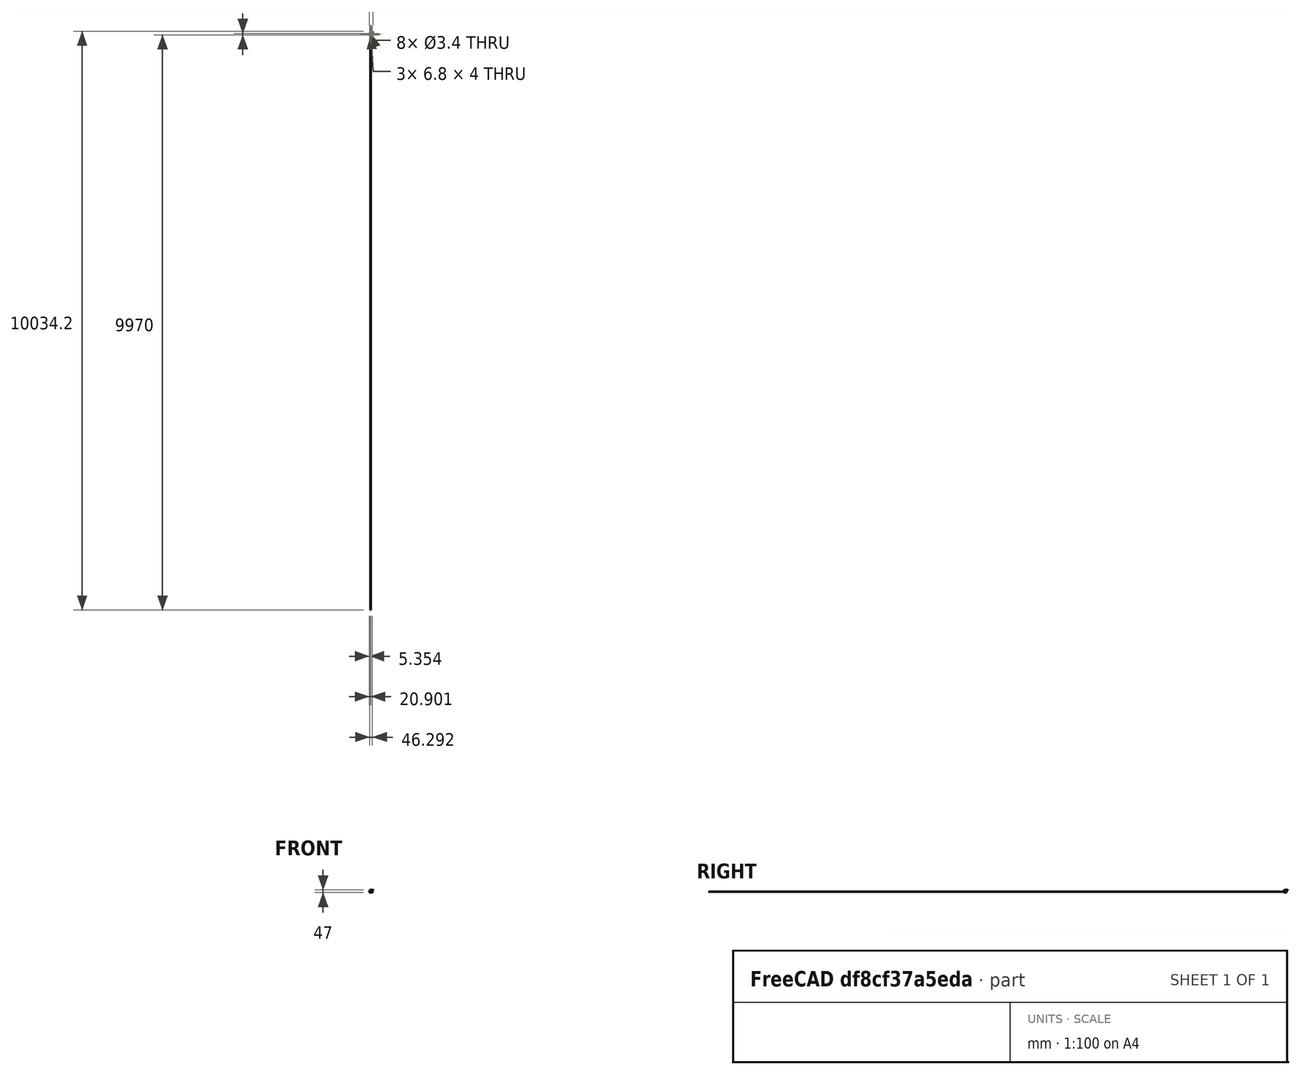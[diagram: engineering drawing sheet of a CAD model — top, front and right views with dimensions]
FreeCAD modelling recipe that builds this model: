
FCSTD DOCUMENT  (FreeCAD 0.14R2935 (Git))
Label: cabeza_cejas
License: CC-BY 3.0
LicenseURL: http://creativecommons.org/licenses/by/3.0/
objects: Sketcher::SketchObject×21, PartDesign::Pocket×15, PartDesign::Chamfer×8, PartDesign::Pad×7, PartDesign::Fillet×6, Part::Box×5, App::DocumentObjectGroup×5, Part::FeaturePython×3, Part::Cylinder×3, Part::Cut×3, Part::Feature×2, Mesh::Feature×1
note: 95 computed .brp shape members not serialized (recipe doc carries the construction recipe); baked Part::Feature solids carry a one-line shape summary decoded from their .brp

FEATURE [Part::Box] Box
  Height = 2
  Length = 10
  Width = 12
FEATURE [Sketcher::SketchObject] Sketch
  Placement = pos=(0,0,2) rot=(0,0,1;0rad)
  Support = -> Box [Face6]
  sketch-geometry (1):
    g0: Circle CenterX=4.90431 CenterY=7.27272 CenterZ=0 NormalX=0 NormalY=0 NormalZ=1 Radius=4.25
  constraints (1):
    c: Radius(g0) = 4.25
FEATURE [PartDesign::Pad] Pad
  Length = 2
  Length2 = 100
  Sketch = -> Sketch
  Type = 0
FEATURE [Sketcher::SketchObject] Sketch001
  ExternalGeometry = -> [Pad]
  Placement = pos=(0,0,4) rot=(0,0,1;0rad)
  Support = -> Pad [Face8]
  sketch-geometry (1):
    g0: Circle CenterX=4.90431 CenterY=7.27272 CenterZ=0 NormalX=0 NormalY=0 NormalZ=1 Radius=2
  constraints (2):
    c: Coincident(g0,g-3)
    c: Radius(g0) = 2
FEATURE [PartDesign::Pocket] Pocket  label="camara"
  Length = 1
  Sketch = -> Sketch001
  Type = 0
FEATURE [App::DocumentObjectGroup] Grupo  label="Camera"
  Group = -> [Box,Pad,Pocket]
FEATURE [Part::FeaturePython] Clone  label="camara001"  # Draft clone (typed FeaturePython)
  Objects = -> [Pocket]
  Placement = pos=(1.5,0,-16) rot=(0,0,1;0rad)
  Scale = (1,1,1)
FEATURE [Part::Cylinder] Cylinder
  Angle = 360
  Height = 2
  Radius = 11.5
FEATURE [Sketcher::SketchObject] Sketch002
  Placement = pos=(0,0,2) rot=(0,0,1;0rad)
  Support = -> Cylinder [Face2]
  sketch-geometry (6):
    g0: LineSegment StartX=-3 StartY=3 StartZ=0 EndX=3 EndY=3 EndZ=0
    g1: LineSegment StartX=3 StartY=3 StartZ=0 EndX=3 EndY=-3 EndZ=0
    g2: LineSegment StartX=3 StartY=-3 StartZ=0 EndX=-3 EndY=-3 EndZ=0
    g3: LineSegment StartX=-3 StartY=-3 StartZ=0 EndX=-3 EndY=3 EndZ=0
    g4: LineSegment [constr] StartX=-3 StartY=3 StartZ=0 EndX=3 EndY=-3 EndZ=0
    g5: LineSegment [constr] StartX=3 StartY=3 StartZ=0 EndX=-3 EndY=-3 EndZ=0
  constraints (16):
    c: Coincident(g0,g1)
    c: Coincident(g1,g2)
    c: Coincident(g2,g3)
    c: Coincident(g3,g0)
    c: Horizontal(g0)
    c: Horizontal(g2)
    c: Vertical(g1)
    c: Vertical(g3)
    c: Equal(g0,g1)
    c: DistanceX(g2) = -6
    c: Coincident(g5,g0)
    c: Coincident(g5,g2)
    c: Coincident(g4,g1)
    c: Coincident(g4,g0)
    c: PointOnObject(g-1,g5)
    c: PointOnObject(g-1,g4)
FEATURE [PartDesign::Pad] Pad001
  Length = 1
  Length2 = 100
  Sketch = -> Sketch002
  Type = 0
FEATURE [Sketcher::SketchObject] Sketch003
  Placement = pos=(0,0,3) rot=(0,0,1;0rad)
  Support = -> Pad001 [Face8]
  sketch-geometry (1):
    g0: Circle CenterX=0 CenterY=0 CenterZ=0 NormalX=0 NormalY=0 NormalZ=1 Radius=2
  constraints (2):
    c: Coincident(g0,g-1)
    c: Radius(g0) = 2
FEATURE [PartDesign::Pocket] Pocket001
  Length = 1
  Sketch = -> Sketch003
  Type = 0
FEATURE [Sketcher::SketchObject] Sketch004
  ExternalGeometry = -> [Pocket001]
  Placement = pos=(0,0,2) rot=(0,0,1;0rad)
  Support = -> Pocket001 [Face2]
  sketch-geometry (28):
    g0: LineSegment StartX=-3 StartY=9.7 StartZ=0 EndX=3 EndY=9.7 EndZ=0
    g1: LineSegment StartX=3 StartY=9.7 StartZ=0 EndX=3 EndY=3.7 EndZ=0
    g2: LineSegment StartX=3 StartY=3.7 StartZ=0 EndX=-3 EndY=3.7 EndZ=0
    g3: LineSegment StartX=-3 StartY=3.7 StartZ=0 EndX=-3 EndY=9.7 EndZ=0
    g4: LineSegment StartX=-9.7 StartY=3 StartZ=0 EndX=-3.7 EndY=3 EndZ=0
    g5: LineSegment StartX=-3.7 StartY=3 StartZ=0 EndX=-3.7 EndY=-3 EndZ=0
    g6: LineSegment StartX=-3.7 StartY=-3 StartZ=0 EndX=-9.7 EndY=-3 EndZ=0
    g7: LineSegment StartX=-9.7 StartY=-3 StartZ=0 EndX=-9.7 EndY=3 EndZ=0
    g8: LineSegment StartX=-3 StartY=-3.7 StartZ=0 EndX=3 EndY=-3.7 EndZ=0
    g9: LineSegment StartX=3 StartY=-3.7 StartZ=0 EndX=3 EndY=-9.7 EndZ=0
    g10: LineSegment StartX=3 StartY=-9.7 StartZ=0 EndX=-3 EndY=-9.7 EndZ=0
    g11: LineSegment StartX=-3 StartY=-9.7 StartZ=0 EndX=-3 EndY=-3.7 EndZ=0
    g12: LineSegment StartX=3.7 StartY=3 StartZ=0 EndX=9.7 EndY=3 EndZ=0
    g13: LineSegment StartX=9.7 StartY=3 StartZ=0 EndX=9.7 EndY=-3 EndZ=0
    g14: LineSegment StartX=9.7 StartY=-3 StartZ=0 EndX=3.7 EndY=-3 EndZ=0
    g15: LineSegment StartX=3.7 StartY=-3 StartZ=0 EndX=3.7 EndY=3 EndZ=0
    g16: LineSegment [constr] StartX=-3 StartY=9.7 StartZ=0 EndX=3 EndY=3.7 EndZ=0
    g17: LineSegment [constr] StartX=3 StartY=9.7 StartZ=0 EndX=-3 EndY=3.7 EndZ=0
    g18: LineSegment [constr] StartX=3.7 StartY=3 StartZ=0 EndX=9.7 EndY=-3 EndZ=0
    g19: LineSegment [constr] StartX=9.7 StartY=3 StartZ=0 EndX=3.7 EndY=-3 EndZ=0
    g20: LineSegment [constr] StartX=-9.7 StartY=3 StartZ=0 EndX=-3.7 EndY=-3 EndZ=0
    g21: LineSegment [constr] StartX=-3.7 StartY=3 StartZ=0 EndX=-9.7 EndY=-3 EndZ=0
    g22: LineSegment [constr] StartX=-3 StartY=-3.7 StartZ=0 EndX=3 EndY=-9.7 EndZ=0
    g23: LineSegment [constr] StartX=3 StartY=-3.7 StartZ=0 EndX=-3 EndY=-9.7 EndZ=0
    g24: GeomPoint [constr] X=0 Y=-6.7 Z=0
    g25: GeomPoint [constr] X=6.7 Y=0 Z=0
    g26: GeomPoint [constr] X=-6.7 Y=0 Z=0
    g27: GeomPoint [constr] X=0 Y=6.7 Z=0
  constraints (72):
    c: Coincident(g0,g1)
    c: Coincident(g1,g2)
    c: Coincident(g2,g3)
    c: Coincident(g3,g0)
    c: Horizontal(g0)
    c: Horizontal(g2)
    c: Vertical(g1)
    c: Vertical(g3)
    c: Equal(g3,g2)
    c: Equal(g2,g-3)
    c: Coincident(g4,g5)
    c: Coincident(g5,g6)
    c: Coincident(g6,g7)
    c: Coincident(g7,g4)
    c: Horizontal(g4)
    c: Horizontal(g6)
    c: Vertical(g5)
    c: Vertical(g7)
    c: Coincident(g8,g9)
    c: Coincident(g9,g10)
    c: Coincident(g10,g11)
    c: Coincident(g11,g8)
    c: Horizontal(g8)
    c: Horizontal(g10)
    c: Vertical(g9)
    c: Vertical(g11)
    c: Coincident(g12,g13)
    c: Coincident(g13,g14)
    c: Coincident(g14,g15)
    c: Coincident(g15,g12)
    c: Horizontal(g12)
    c: Horizontal(g14)
    c: Vertical(g13)
    c: Vertical(g15)
    c: Equal(g12,g15)
    c: Equal(g15,g8)
    c: Equal(g8,g9)
    c: Equal(g9,g6)
    c: Equal(g6,g5)
    c: Equal(g2,g12)
    c: Coincident(g23,g10)
    c: Coincident(g22,g8)
    c: Coincident(g23,g8)
    c: Coincident(g22,g9)
    c: PointOnObject(g24,g-2)
    c: PointOnObject(g24,g23)
    c: PointOnObject(g24,g22)
    c: Coincident(g19,g12)
    c: Coincident(g18,g13)
    c: Coincident(g18,g12)
    c: Coincident(g19,g14)
    c: Coincident(g16,g1)
    c: Coincident(g17,g0)
    c: Coincident(g17,g2)
    c: Coincident(g16,g0)
    c: Coincident(g21,g4)
    c: Coincident(g20,g4)
    c: Coincident(g21,g6)
    c: Coincident(g20,g5)
    c: PointOnObject(g25,g-1)
    c: PointOnObject(g26,g-1)
    c: PointOnObject(g27,g-2)
    c: PointOnObject(g26,g20)
    c: PointOnObject(g26,g21)
    c: PointOnObject(g25,g19)
    c: PointOnObject(g25,g18)
    c: PointOnObject(g27,g16)
    c: PointOnObject(g27,g17)
    c: Distance(g-4,g4) = 0.7
    c: Distance(g-4,g8) = 0.7
    c: Distance(g-5,g14) = 0.7
    c: Distance(g2,g-4) = 0.7
FEATURE [PartDesign::Pad] Pad002
  Length = 1
  Length2 = 100
  Sketch = -> Sketch004
  Type = 0
FEATURE [Sketcher::SketchObject] Sketch005
  ExternalGeometry = -> [Pad002]
  Placement = pos=(0,0,3) rot=(0,0,1;0rad)
  Support = -> Pad002 [Face26]
  sketch-geometry (4):
    g0: Circle CenterX=0 CenterY=6.61559 CenterZ=0 NormalX=0 NormalY=0 NormalZ=1 Radius=2
    g1: Circle CenterX=-6.61558 CenterY=0 CenterZ=0 NormalX=0 NormalY=0 NormalZ=1 Radius=2
    g2: Circle CenterX=6.71215 CenterY=0 CenterZ=0 NormalX=0 NormalY=0 NormalZ=1 Radius=2
    g3: Circle CenterX=0 CenterY=-6.71214 CenterZ=0 NormalX=0 NormalY=0 NormalZ=1 Radius=2
  constraints (8):
    c: Equal(g1,g0)
    c: Equal(g0,g-3)
    c: Equal(g-3,g2)
    c: Equal(g2,g3)
    c: PointOnObject(g2,g-1)
    c: PointOnObject(g0,g-2)
    c: PointOnObject(g1,g-1)
    c: PointOnObject(g3,g-2)
FEATURE [PartDesign::Pocket] Pocket002
  Length = 1
  Sketch = -> Sketch005
  Type = 0
FEATURE [Part::FeaturePython] Clone001  label="ojo001"  # Draft clone (typed FeaturePython)
  Objects = -> [Pocket002]
  Placement = pos=(-7,-6,-13) rot=(0,0,1;0rad)
  Scale = (1,1,1)
FEATURE [App::DocumentObjectGroup] Grupo001  label="ojo"
  Group = -> [Cylinder,Pad001,Pocket001,Pad002,Pocket002]
FEATURE [Part::FeaturePython] Clone002  label="ojo002"  # Draft clone (typed FeaturePython)
  Objects = -> [Pocket002]
  Placement = pos=(21,-7,-13) rot=(0,0,1;0rad)
  Scale = (1,1,1)
FEATURE [Part::Box] Box001
  Height = 4
  Length = 35
  Placement = pos=(-11,-31,-17) rot=(0,0,1;0rad)
  Width = 47
FEATURE [Mesh::Feature] _g_servo  label="9g_servo"
  Placement = pos=(0,-7,-24) rot=(0.57735,0.57735,0.57735;2.0944rad)
FEATURE [Sketcher::SketchObject] Sketch006
  ExternalGeometry = -> [Box001]
  Placement = pos=(-11,-31,-17) rot=(1,0,0;3.14159rad)
  Support = -> Box001 [Face5]
  sketch-geometry (9):
    g0: LineSegment StartX=6.5 StartY=-7.91944 StartZ=0 EndX=13.302 EndY=-7.91944 EndZ=0
    g1: LineSegment StartX=13.302 StartY=-7.91944 StartZ=0 EndX=13.302 EndY=-11.9194 EndZ=0
    g2: LineSegment StartX=13.302 StartY=-11.9194 StartZ=0 EndX=6.5 EndY=-11.9194 EndZ=0
    g3: LineSegment StartX=6.5 StartY=-11.9194 StartZ=0 EndX=6.5 EndY=-7.91944 EndZ=0
    g4: LineSegment StartX=6.5 StartY=-35.9194 StartZ=0 EndX=13.302 EndY=-35.9194 EndZ=0
    g5: LineSegment StartX=13.302 StartY=-35.9194 StartZ=0 EndX=13.302 EndY=-39.9194 EndZ=0
    g6: LineSegment StartX=13.302 StartY=-39.9194 StartZ=0 EndX=6.5 EndY=-39.9194 EndZ=0
    g7: LineSegment StartX=6.5 StartY=-39.9194 StartZ=0 EndX=6.5 EndY=-35.9194 EndZ=0
    g8: LineSegment [constr] StartX=6.5 StartY=0 StartZ=0 EndX=6.5 EndY=-47 EndZ=0
  constraints (27):
    c: Coincident(g0,g1)
    c: Coincident(g1,g2)
    c: Coincident(g2,g3)
    c: Coincident(g3,g0)
    c: Horizontal(g0)
    c: Horizontal(g2)
    c: Vertical(g1)
    c: Vertical(g3)
    c: Coincident(g4,g5)
    c: Coincident(g5,g6)
    c: Coincident(g6,g7)
    c: Coincident(g7,g4)
    c: Horizontal(g4)
    c: Horizontal(g6)
    c: Vertical(g5)
    c: Vertical(g7)
    c: Equal(g2,g4)
    c: Vertical(g8)
    c: PointOnObject(g8,g-3)
    c: PointOnObject(g8,g-1)
    c: PointOnObject(g0,g8)
    c: PointOnObject(g4,g8)
    c: Equal(g1,g5)
    c: DistanceY(g1) = -4
    c: Distance(g2,g4) = 24
    c: Distance(g6,g8) = 7.08056
    c: Distance(g-3,g8) = 6.5
FEATURE [PartDesign::Pad] Pad003
  Length = 14
  Length2 = 100
  Placement = pos=(-11,-31,-17) rot=(0,0,1;0rad)
  Sketch = -> Sketch006
  Type = 0
FEATURE [Sketcher::SketchObject] Sketch007
  ExternalGeometry = -> [Pad003]
  Placement = pos=(2.30204,-31,-17) rot=(0.57735,0.57735,0.57735;2.0944rad)
  Support = -> Pad003 [Face7]
  sketch-geometry (3):
    g0: Circle CenterX=9.93523 CenterY=-7.03791 CenterZ=0 NormalX=0 NormalY=0 NormalZ=1 Radius=1.64716
    g1: Circle CenterX=37.8885 CenterY=-7.03791 CenterZ=0 NormalX=0 NormalY=0 NormalZ=1 Radius=1.53113
    g2: LineSegment [constr] StartX=35.9194 StartY=-7.03791 StartZ=0 EndX=11.9194 EndY=-7.03791 EndZ=0
  constraints (5):
    c: PointOnObject(g2,g-3)
    c: Horizontal(g2)
    c: PointOnObject(g2,g-4)
    c: PointOnObject(g0,g2)
    c: PointOnObject(g1,g2)
FEATURE [PartDesign::Pocket] Pocket003
  Length = 7
  Placement = pos=(-11,-31,-17) rot=(0,0,1;0rad)
  Sketch = -> Sketch007
  Type = 0
FEATURE [Sketcher::SketchObject] Sketch008
  ExternalGeometry = -> [Pocket003]
  Placement = pos=(-11,-31,-17) rot=(1,0,0;3.14159rad)
  Support = -> Pocket003 [Face5]
  sketch-geometry (6):
    g0: ArcOfCircle CenterX=31.6459 CenterY=-23.9498 CenterZ=0 NormalX=0 NormalY=0 NormalZ=1 Radius=11.5 StartAngle=5.00835 EndAngle=7.55802
    g1: LineSegment [constr] StartX=35 StartY=-12.9498 StartZ=0 EndX=0 EndY=-12.9498 EndZ=0
    g2: LineSegment [constr] StartX=35 StartY=-34.9498 StartZ=0 EndX=0 EndY=-34.9498 EndZ=0
    g3: ArcOfCircle CenterX=3.3541 CenterY=-23.9498 CenterZ=0 NormalX=0 NormalY=0 NormalZ=1 Radius=11.5 StartAngle=1.86676 EndAngle=4.41643
    g4: LineSegment StartX=35 StartY=-12.9498 StartZ=0 EndX=35 EndY=-34.9498 EndZ=0
    g5: LineSegment StartX=0 StartY=-12.9498 StartZ=0 EndX=0 EndY=-34.9498 EndZ=0
  constraints (20):
    c: PointOnObject(g0,g-3)
    c: PointOnObject(g0,g-3)
    c: Distance(g0,g0) = 22
    c: Radius(g0) = 11.5
    c: Horizontal(g1)
    c: Horizontal(g2)
    c: Distance(g-3,g0) = 12.9498
    c: Coincident(g1,g0)
    c: PointOnObject(g1,g-2)
    c: Coincident(g2,g0)
    c: PointOnObject(g2,g-2)
    c: Coincident(g3,g2)
    c: Coincident(g3,g1)
    c: Equal(g0,g3)
    c: Vertical(g4)
    c: Coincident(g4,g0)
    c: Coincident(g4,g0)
    c: Vertical(g5)
    c: Coincident(g5,g1)
    c: Coincident(g5,g2)
FEATURE [PartDesign::Pad] Pad004
  Length = 4
  Length2 = 100
  Placement = pos=(-11,-31,-17) rot=(0,0,1;0rad)
  Reversed = true
  Sketch = -> Sketch008
  Type = 0
FEATURE [Sketcher::SketchObject] Sketch009
  ExternalGeometry = -> [Pad004]
  Placement = pos=(-11,-31,-13) rot=(0,0,1;0rad)
  Support = -> Pad004 [Face4]
  sketch-geometry (6):
    g0: Circle CenterX=17.5 CenterY=38.5843 CenterZ=0 NormalX=0 NormalY=0 NormalZ=1 Radius=4.5
    g1: LineSegment [constr] StartX=0 StartY=38.5843 StartZ=0 EndX=17.5 EndY=38.5843 EndZ=0
    g2: LineSegment [constr] StartX=17.5 StartY=38.5843 StartZ=0 EndX=35 EndY=38.5843 EndZ=0
    g3: Circle CenterX=-5.6459 CenterY=23.9498 CenterZ=0 NormalX=0 NormalY=0 NormalZ=1 Radius=1.7
    g4: Circle CenterX=40.6459 CenterY=23.9498 CenterZ=0 NormalX=0 NormalY=0 NormalZ=1 Radius=1.7
    g5: LineSegment [constr] StartX=-8.1459 StartY=23.9498 StartZ=0 EndX=43.1459 EndY=23.9498 EndZ=0
  constraints (19):
    c: Horizontal(g1)
    c: Horizontal(g2)
    c: PointOnObject(g1,g-2)
    c: PointOnObject(g2,g-3)
    c: Coincident(g2,g0)
    c: Coincident(g1,g0)
    c: Equal(g1,g2)
    c: Radius(g0) = 4.5
    c: DistanceY(g-1,g2) = 38.5843
    c: Horizontal(g5)
    c: PointOnObject(g5,g-5)
    c: PointOnObject(g5,g-4)
    c: PointOnObject(g3,g5)
    c: PointOnObject(g4,g5)
    c: Radius(g4) = 1.7
    c: Radius(g3) = 1.7
    c: Distance(g3,g5) = 2.5
    c: Distance(g4,g5) = 2.5
    c: PointOnObject(g-5,g5)
FEATURE [PartDesign::Pocket] Pocket004
  Length = 4
  Placement = pos=(-11,-31,-17) rot=(0,0,1;0rad)
  Sketch = -> Sketch009
  Type = 0
FEATURE [Part::Feature] Pocket004001  label="Pocket005"
  shape: bbox 51.29 x 47 x 18 mm, 26 faces (baked)
FEATURE [PartDesign::Chamfer] Chamfer
  Base = -> Pocket004001 [Edge6]
  Size = 10
FEATURE [PartDesign::Chamfer] Chamfer001
  Base = -> Chamfer [Edge3]
  Size = 10
FEATURE [PartDesign::Fillet] Fillet
  Base = -> Chamfer001 [Edge3]
  Radius = 10
FEATURE [PartDesign::Fillet] Fillet001
  Base = -> Fillet [Edge3]
  Radius = 10
FEATURE [PartDesign::Fillet] Fillet002
  Base = -> Fillet001 [Edge45]
  Radius = 3
FEATURE [PartDesign::Fillet] Fillet003
  Base = -> Fillet002 [Edge43]
  Radius = 3
FEATURE [PartDesign::Chamfer] Chamfer002
  Base = -> Fillet003 [Edge46]
  Size = 10
FEATURE [PartDesign::Chamfer] Chamfer003
  Base = -> Chamfer002 [Edge29]
  Size = 10
FEATURE [Sketcher::SketchObject] Sketch010
  ExternalGeometry = -> [Chamfer003]
  Placement = pos=(0,0,-13) rot=(0,0,1;0rad)
  Support = -> Chamfer003 [Face29]
  sketch-geometry (9):
    g0: LineSegment [constr] StartX=-16.6459 StartY=-7.0502 StartZ=0 EndX=29.6459 EndY=-7.0502 EndZ=0
    g1: Circle CenterX=3.3541 CenterY=-7.0502 CenterZ=0 NormalX=0 NormalY=0 NormalZ=1 Radius=1.7
    g2: Circle CenterX=9.6459 CenterY=-7.0502 CenterZ=0 NormalX=0 NormalY=0 NormalZ=1 Radius=1.7
    g3: LineSegment [constr] StartX=-1 StartY=-7.0502 StartZ=0 EndX=-1 EndY=-31 EndZ=0
    g4: LineSegment [constr] StartX=14 StartY=-7.0502 StartZ=0 EndX=14 EndY=-31 EndZ=0
    g5: LineSegment StartX=-1 StartY=-23.5 StartZ=0 EndX=14 EndY=-23.5 EndZ=0
    g6: LineSegment StartX=14 StartY=-23.5 StartZ=0 EndX=14 EndY=-26.5 EndZ=0
    g7: LineSegment StartX=14 StartY=-26.5 StartZ=0 EndX=-1 EndY=-26.5 EndZ=0
    g8: LineSegment StartX=-1 StartY=-26.5 StartZ=0 EndX=-1 EndY=-23.5 EndZ=0
  constraints (27):
    c: Horizontal(g0)
    c: Coincident(g0,g-4)
    c: Coincident(g0,g-3)
    c: PointOnObject(g1,g0)
    c: PointOnObject(g2,g0)
    c: Radius(g2) = 1.7
    c: Radius(g1) = 1.7
    c: Distance(g0,g1) = 20
    c: Distance(g2,g0) = 20
    c: Vertical(g3)
    c: Coincident(g3,g-5)
    c: PointOnObject(g3,g0)
    c: Vertical(g4)
    c: Coincident(g4,g-5)
    c: PointOnObject(g4,g0)
    c: Coincident(g5,g6)
    c: Coincident(g6,g7)
    c: Coincident(g7,g8)
    c: Coincident(g8,g5)
    c: Horizontal(g5)
    c: Horizontal(g7)
    c: Vertical(g6)
    c: Vertical(g8)
    c: DistanceY(g6) = -3
    c: PointOnObject(g7,g3)
    c: PointOnObject(g6,g4)
    c: Distance(g7,g3) = 4.5
FEATURE [PartDesign::Pocket] Pocket004002
  Length = 5
  Sketch = -> Sketch010
  Type = 0
FEATURE [Sketcher::SketchObject] Sketch011
  Placement = pos=(0,8.91944,0) rot=(0,0.707107,0.707107;3.14159rad)
  Support = -> Pocket004002 [Face18]
  sketch-geometry (4):
    g0: LineSegment StartX=-1.74892 StartY=-26.7435 StartZ=0 EndX=3.95108 EndY=-26.7435 EndZ=0
    g1: LineSegment StartX=3.95108 StartY=-26.7435 StartZ=0 EndX=3.95108 EndY=-29.3435 EndZ=0
    g2: LineSegment StartX=3.95108 StartY=-29.3435 StartZ=0 EndX=-1.74892 EndY=-29.3435 EndZ=0
    g3: LineSegment StartX=-1.74892 StartY=-29.3435 StartZ=0 EndX=-1.74892 EndY=-26.7435 EndZ=0
  constraints (10):
    c: Coincident(g0,g1)
    c: Coincident(g1,g2)
    c: Coincident(g2,g3)
    c: Coincident(g3,g0)
    c: Horizontal(g0)
    c: Horizontal(g2)
    c: Vertical(g1)
    c: Vertical(g3)
    c: DistanceY(g1) = -2.6
    c: DistanceX(g2) = -5.7
FEATURE [PartDesign::Pocket] Pocket004003
  Length = 5
  Sketch = -> Sketch011
  Type = 1
FEATURE [Sketcher::SketchObject] Sketch012
  ExternalGeometry = -> [Pocket004003]
  Placement = pos=(0,0,-31) rot=(1,0,0;3.14159rad)
  Support = -> Pocket004003 [Face37]
  sketch-geometry (6):
    g0: LineSegment [constr] StartX=-4.5 StartY=23.0806 StartZ=0 EndX=2.30204 EndY=19.0806 EndZ=0
    g1: LineSegment [constr] StartX=2.30204 StartY=23.0806 StartZ=0 EndX=-4.5 EndY=19.0806 EndZ=0
    g2: Circle CenterX=-1.09898 CenterY=21.0806 CenterZ=0 NormalX=0 NormalY=0 NormalZ=1 Radius=1.7
    g3: LineSegment [constr] StartX=-4.5 StartY=-4.91944 StartZ=0 EndX=2.30204 EndY=-8.91944 EndZ=0
    g4: LineSegment [constr] StartX=2.30204 StartY=-4.91944 StartZ=0 EndX=-4.5 EndY=-8.91944 EndZ=0
    g5: Circle CenterX=-1.09898 CenterY=-6.91944 CenterZ=0 NormalX=0 NormalY=0 NormalZ=1 Radius=1.7
  constraints (14):
    c: Coincident(g1,g-4)
    c: Coincident(g1,g-3)
    c: Coincident(g0,g-4)
    c: Coincident(g0,g-3)
    c: PointOnObject(g2,g1)
    c: PointOnObject(g2,g0)
    c: Radius(g2) = 1.7
    c: Coincident(g4,g-6)
    c: Coincident(g4,g-5)
    c: Coincident(g3,g-6)
    c: Coincident(g3,g-5)
    c: PointOnObject(g5,g4)
    c: PointOnObject(g5,g3)
    c: Radius(g5) = 1.7
FEATURE [PartDesign::Pocket] Pocket004004
  Length = 4
  Sketch = -> Sketch012
  Type = 0
FEATURE [Part::Box] Box002
  Height = 26
  Length = 36
  Placement = pos=(-12,-31,-43) rot=(0,0,1;0rad)
  Width = 47
FEATURE [PartDesign::Pocket] Pocket004005
  Length = 4
  Sketch = -> Sketch012
  Type = 0
FEATURE [Part::Feature] Pocket004006  label="cara"
  shape: bbox 51.29 x 47 x 18 mm, 50 faces (baked)
FEATURE [PartDesign::Fillet] Fillet004
  Base = -> Box002 [Edge7]
  Placement = pos=(-12,-31,-43) rot=(0,0,1;0rad)
  Radius = 17
FEATURE [PartDesign::Fillet] Fillet005
  Base = -> Fillet004 [Edge15]
  Placement = pos=(-12,-31,-43) rot=(0,0,1;0rad)
  Radius = 17
FEATURE [PartDesign::Chamfer] Chamfer004
  Base = -> Fillet005 [Edge16]
  Placement = pos=(-12,-31,-43) rot=(0,0,1;0rad)
  Size = 10
FEATURE [PartDesign::Chamfer] Chamfer005
  Base = -> Chamfer004 [Edge16]
  Placement = pos=(-12,-31,-43) rot=(0,0,1;0rad)
  Size = 10
FEATURE [Part::Box] Box003
  Height = 26
  Length = 36
  Placement = pos=(-12,-31,-43) rot=(0,0,1;0rad)
  Width = 10
FEATURE [Part::Cut] Cut
  Base = -> Chamfer005
  Tool = -> Box003
FEATURE [Sketcher::SketchObject] Sketch013
  ExternalGeometry = -> [Cut]
  Placement = pos=(0,-21,0) rot=(1,0,0;1.5708rad)
  Support = -> Cut [Face7]
  sketch-geometry (4):
    g0: LineSegment StartX=-9 StartY=-17 StartZ=0 EndX=21 EndY=-17 EndZ=0
    g1: LineSegment StartX=21 StartY=-17 StartZ=0 EndX=21 EndY=-40 EndZ=0
    g2: LineSegment StartX=21 StartY=-40 StartZ=0 EndX=-9 EndY=-40 EndZ=0
    g3: LineSegment StartX=-9 StartY=-40 StartZ=0 EndX=-9 EndY=-17 EndZ=0
  constraints (12):
    c: Coincident(g0,g1)
    c: Coincident(g1,g2)
    c: Coincident(g2,g3)
    c: Coincident(g3,g0)
    c: Horizontal(g0)
    c: Horizontal(g2)
    c: Vertical(g1)
    c: Vertical(g3)
    c: PointOnObject(g0,g-5)
    c: Distance(g-5,g0) = 3
    c: Distance(g-5,g0) = 3
    c: Distance(g2,g-6) = 3
FEATURE [PartDesign::Pocket] Pocket004007
  Length = 27
  Sketch = -> Sketch013
  Type = 0
FEATURE [Sketcher::SketchObject] Sketch014
  ExternalGeometry = -> [Pocket004007]
  Placement = pos=(0,0,-17) rot=(0,0,1;0rad)
  Support = -> Pocket004007 [Face1]
  sketch-geometry (4):
    g0: LineSegment StartX=-0.588067 StartY=13.0845 StartZ=0 EndX=12.9735 EndY=13.0845 EndZ=0
    g1: LineSegment StartX=12.9735 StartY=13.0845 StartZ=0 EndX=12.9735 EndY=6 EndZ=0
    g2: LineSegment StartX=12.9735 StartY=6 StartZ=0 EndX=-0.588067 EndY=6 EndZ=0
    g3: LineSegment StartX=-0.588067 StartY=6 StartZ=0 EndX=-0.588067 EndY=13.0845 EndZ=0
  constraints (9):
    c: Coincident(g0,g1)
    c: Coincident(g1,g2)
    c: Coincident(g2,g3)
    c: Coincident(g3,g0)
    c: Horizontal(g0)
    c: Horizontal(g2)
    c: Vertical(g1)
    c: Vertical(g3)
    c: PointOnObject(g2,g-3)
FEATURE [PartDesign::Pocket] Pocket004008
  Length = 23
  Sketch = -> Sketch014
  Type = 0
FEATURE [Sketcher::SketchObject] Sketch015
  ExternalGeometry = -> [Pocket004008]
  Placement = pos=(0,0,-43) rot=(1,0,0;3.14159rad)
  Support = -> Pocket004008 [Face15]
  sketch-geometry (8):
    g0: LineSegment StartX=-22 StartY=21 StartZ=0 EndX=-12 EndY=21 EndZ=0
    g1: LineSegment StartX=-12 StartY=21 StartZ=0 EndX=-12 EndY=1 EndZ=0
    g2: LineSegment StartX=-12 StartY=1 StartZ=0 EndX=-22 EndY=1 EndZ=0
    g3: LineSegment StartX=-22 StartY=1 StartZ=0 EndX=-22 EndY=21 EndZ=0
    g4: LineSegment StartX=34 StartY=21 StartZ=0 EndX=24 EndY=21 EndZ=0
    g5: LineSegment StartX=24 StartY=21 StartZ=0 EndX=24 EndY=1 EndZ=0
    g6: LineSegment StartX=24 StartY=1 StartZ=0 EndX=34 EndY=1 EndZ=0
    g7: LineSegment StartX=34 StartY=1 StartZ=0 EndX=34 EndY=21 EndZ=0
  constraints (22):
    c: Coincident(g0,g1)
    c: Coincident(g1,g2)
    c: Coincident(g2,g3)
    c: Coincident(g3,g0)
    c: Horizontal(g0)
    c: Horizontal(g2)
    c: Vertical(g1)
    c: Vertical(g3)
    c: Coincident(g-3,g0)
    c: Coincident(g1,g-3)
    c: Coincident(g4,g5)
    c: Coincident(g5,g6)
    c: Coincident(g6,g7)
    c: Coincident(g7,g4)
    c: Horizontal(g4)
    c: Horizontal(g6)
    c: Vertical(g5)
    c: Vertical(g7)
    c: Coincident(g5,g-4)
    c: Coincident(g4,g-4)
    c: Equal(g0,g4)
    c: DistanceX(g2) = -10
FEATURE [PartDesign::Pad] Pad005
  Length = 25
  Length2 = 100
  Reversed = true
  Sketch = -> Sketch015
  Type = 0
FEATURE [PartDesign::Chamfer] Chamfer006
  Base = -> Pad005 [Edge48]
  Size = 9
FEATURE [PartDesign::Chamfer] Chamfer007
  Base = -> Chamfer006 [Edge67]
  Size = 9
FEATURE [Sketcher::SketchObject] Sketch016
  ExternalGeometry = -> [Chamfer007]
  Placement = pos=(2.5,0,-2.5) rot=(0.357407,-0.357407,-0.862856;1.71777rad)
  Support = -> Chamfer007 [Face21]
  sketch-geometry (4):
    g0: LineSegment StartX=4 StartY=-28.1482 StartZ=0 EndX=19 EndY=-28.1482 EndZ=0
    g1: LineSegment StartX=19 StartY=-28.1482 StartZ=0 EndX=19 EndY=-31.1482 EndZ=0
    g2: LineSegment StartX=19 StartY=-31.1482 StartZ=0 EndX=4 EndY=-31.1482 EndZ=0
    g3: LineSegment StartX=4 StartY=-31.1482 StartZ=0 EndX=4 EndY=-28.1482 EndZ=0
  constraints (12):
    c: Coincident(g0,g1)
    c: Coincident(g1,g2)
    c: Coincident(g2,g3)
    c: Coincident(g3,g0)
    c: Horizontal(g0)
    c: Horizontal(g2)
    c: Vertical(g1)
    c: Vertical(g3)
    c: Distance(g2,g-3) = 3.5
    c: DistanceX(g2) = -15
    c: Distance(g1,g-4) = 2
    c: DistanceY(g1) = -3
FEATURE [PartDesign::Pocket] Pocket004009
  Length = 10
  Sketch = -> Sketch016
  Type = 0
FEATURE [Sketcher::SketchObject] Sketch017
  ExternalGeometry = -> [Pocket004009]
  Placement = pos=(3.5,0,3.5) rot=(0.357407,0.357407,0.862856;1.71777rad)
  Support = -> Pocket004009 [Face3]
  sketch-geometry (4):
    g0: LineSegment StartX=-18 StartY=-37.1335 StartZ=0 EndX=-3 EndY=-37.1335 EndZ=0
    g1: LineSegment StartX=-3 StartY=-37.1335 StartZ=0 EndX=-3 EndY=-40.1335 EndZ=0
    g2: LineSegment StartX=-3 StartY=-40.1335 StartZ=0 EndX=-18 EndY=-40.1335 EndZ=0
    g3: LineSegment StartX=-18 StartY=-40.1335 StartZ=0 EndX=-18 EndY=-37.1335 EndZ=0
  constraints (12):
    c: Coincident(g0,g1)
    c: Coincident(g1,g2)
    c: Coincident(g2,g3)
    c: Coincident(g3,g0)
    c: Horizontal(g0)
    c: Horizontal(g2)
    c: Vertical(g1)
    c: Vertical(g3)
    c: DistanceX(g2) = -15
    c: Distance(g0,g-3) = 3
    c: Distance(g2,g-4) = 3
    c: DistanceY(g1) = -3
FEATURE [PartDesign::Pocket] Pocket004010
  Length = 15
  Sketch = -> Sketch017
  Type = 0
FEATURE [Sketcher::SketchObject] Sketch018
  ExternalGeometry = -> [Pocket004010]
  Placement = pos=(0,16,0) rot=(0,0.707107,0.707107;3.14159rad)
  Support = -> Pocket004010 [Face24]
  sketch-geometry (4):
    g0: LineSegment StartX=-7 StartY=-17 StartZ=0 EndX=-5 EndY=-17 EndZ=0
    g1: LineSegment StartX=-5 StartY=-17 StartZ=0 EndX=-5 EndY=-43 EndZ=0
    g2: LineSegment StartX=-5 StartY=-43 StartZ=0 EndX=-7 EndY=-43 EndZ=0
    g3: LineSegment StartX=-7 StartY=-43 StartZ=0 EndX=-7 EndY=-17 EndZ=0
  constraints (11):
    c: Coincident(g0,g1)
    c: Coincident(g1,g2)
    c: Coincident(g2,g3)
    c: Coincident(g3,g0)
    c: Horizontal(g0)
    c: Horizontal(g2)
    c: Vertical(g1)
    c: Vertical(g3)
    c: Coincident(g1,g-4)
    c: Coincident(g0,g-4)
    c: Coincident(g0,g-3)
FEATURE [PartDesign::Pad] Pad006
  Length = 10
  Length2 = 100
  Sketch = -> Sketch018
  Type = 0
FEATURE [Sketcher::SketchObject] Sketch019
  ExternalGeometry = -> [Pad006]
  Placement = pos=(7,0,0) rot=(0.57735,0.57735,0.57735;2.0944rad)
  Support = -> Pad006 [Face35]
  sketch-geometry (3):
    g0: LineSegment StartX=16 StartY=-17 StartZ=0 EndX=26 EndY=-43 EndZ=0
    g1: LineSegment StartX=26 StartY=-43 StartZ=0 EndX=26 EndY=-17 EndZ=0
    g2: LineSegment StartX=26 StartY=-17 StartZ=0 EndX=16 EndY=-17 EndZ=0
  constraints (6):
    c: Coincident(g0,g1)
    c: Coincident(g1,g2)
    c: Coincident(g2,g0)
    c: Coincident(g1,g-4)
    c: Coincident(g0,g-3)
    c: Coincident(g0,g-4)
FEATURE [PartDesign::Pocket] Pocket004011  label="cabeza"
  Length = 5
  Sketch = -> Sketch019
  Type = 0
FEATURE [App::DocumentObjectGroup] Grupo002  label="craneo"
  Group = -> [Fillet004,Fillet005,Chamfer004,Cut,Pocket004007,Pocket004008,Pad005,Chamfer006,Chamfer007,Pocket004009,Pocket004010,Pad006,Pocket004011,Box002]
FEATURE [App::DocumentObjectGroup] Grupo003  label="Rostro"
  Group = -> [Pad003,Pocket003,Pad004,Pocket004,Pocket004001,Chamfer,Chamfer001,Fillet,Fillet001,Fillet002,Fillet003,Chamfer002,Chamfer003,Pocket004002,Pocket004003,Pocket004004,Pocket004005,Pocket004006,Box001]
FEATURE [App::DocumentObjectGroup] Grupo004  label="Montaje"
  Group = -> [Grupo,Clone,Clone001,Grupo001,Clone002,_g_servo]
FEATURE [Part::Cylinder] Cylinder001
  Angle = 360
  Height = 10
  Placement = pos=(-7,-7,-16) rot=(0,0,1;0rad)
  Radius = 13
FEATURE [Sketcher::SketchObject] Sketch020
  ExternalGeometry = -> [Cylinder001]
  Placement = pos=(-7,-7,-6) rot=(0,0,1;0rad)
  Support = -> Cylinder001 [Face2]
  sketch-geometry (6):
    g0: ArcOfCircle CenterX=0 CenterY=0 CenterZ=0 NormalX=0 NormalY=0 NormalZ=1 Radius=11.0431 StartAngle=0 EndAngle=3.14159
    g1: LineSegment StartX=-11.0431 StartY=0 StartZ=0 EndX=-15.3539 EndY=0 EndZ=0
    g2: LineSegment StartX=-15.3539 StartY=0 StartZ=0 EndX=-15.3539 EndY=-14.2255 EndZ=0
    g3: LineSegment StartX=-15.3539 StartY=-14.2255 StartZ=0 EndX=14.9257 EndY=-14.2255 EndZ=0
    g4: LineSegment StartX=14.9257 StartY=-14.2255 StartZ=0 EndX=14.9257 EndY=0 EndZ=0
    g5: LineSegment StartX=14.9257 StartY=0 StartZ=0 EndX=11.0431 EndY=0 EndZ=0
  constraints (14):
    c: PointOnObject(g0,g-1)
    c: PointOnObject(g0,g-1)
    c: Coincident(g0,g-1)
    c: Horizontal(g1)
    c: Coincident(g1,g2)
    c: Coincident(g2,g3)
    c: Horizontal(g3)
    c: Coincident(g3,g4)
    c: Coincident(g4,g5)
    c: Coincident(g5,g0)
    c: Horizontal(g5)
    c: Coincident(g1,g0)
    c: Vertical(g2)
    c: Vertical(g4)
FEATURE [PartDesign::Pocket] Pocket004012
  Length = 10
  Placement = pos=(-7,-7,-16) rot=(0,0,1;0rad)
  Sketch = -> Sketch020
  Type = 0
FEATURE [Part::Cylinder] Cylinder002
  Angle = 360
  Height = 5
  Placement = pos=(-7,-7,-16) rot=(0,0,1;0rad)
  Radius = 12.5
FEATURE [Part::Cut] Cut001
  Base = -> Pocket004012
  Tool = -> Cylinder002
FEATURE [Part::Box] Box004
  Height = 4
  Length = 19
  Placement = pos=(-11,-12,-17) rot=(0,0,1;0rad)
  Width = 20
FEATURE [Part::Cut] Cut002
  Base = -> Cut001
  Tool = -> Box004
